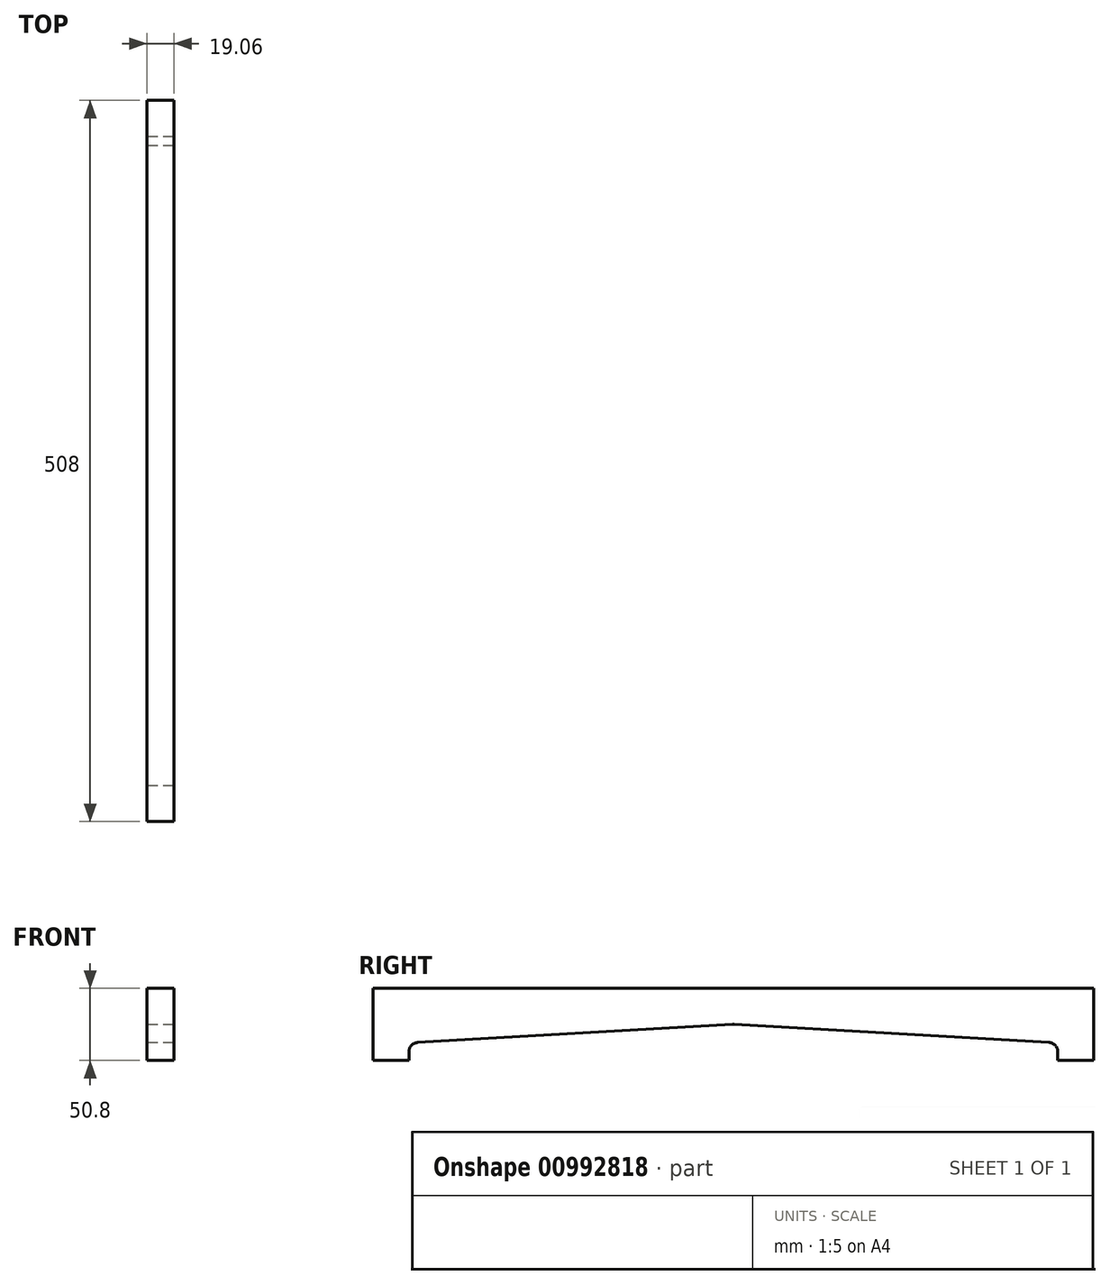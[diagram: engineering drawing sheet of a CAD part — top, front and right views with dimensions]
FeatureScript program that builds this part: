
annotation { "Feature Type Name" : "Feature", "Feature Type Description" : "" }
export const myFeature = defineFeature(function(context is Context, id is Id, definition is map)
    precondition{}
    {
        {
            var Q0;
            Q0=qCreatedBy(makeId("Front.planeOp"),FACE);
            var sketch = newSketch(context, id + "F0", { "sketchPlane" : qUnion([Q0])});
            skLineSegment(sketch, "E0", {"start": v(0, 25.4) * mm, "end": v(0, -25.4) * mm, "construction": true});
            skLineSegment(sketch, "E1", {"start": v(9.52, 0) * mm, "end": v(-9.52, 0) * mm, "construction": true});
            skLineSegment(sketch, "E2.bottom", {"start": v(9.52, 25.4) * mm, "end": v(-9.52, 25.4) * mm});
            skLineSegment(sketch, "E2.top", {"start": v(9.52, -25.4) * mm, "end": v(-9.52, -25.4) * mm});
            skLineSegment(sketch, "E2.left", {"start": v(9.52, 25.4) * mm, "end": v(9.52, -25.4) * mm});
            skLineSegment(sketch, "E2.right", {"start": v(-9.52, 25.4) * mm, "end": v(-9.52, -25.4) * mm});
            skPoint(sketch, "E2.middle", {"position": v(0, 0) * mm});
            skSolve(sketch);
        }
        {
            var Q0;
            Q0 = qSketchRegion(id + "F0", true);
            extrude(context, id + "F1", {"entities" : qUnion([Q0]), "endBound" : BoundingType.SYMMETRIC, "depth" : 508 * mm, "offsetDistance" : 25.4 * mm});
        }
        {
            var Q0;
            Q0=makeQuery(id+"F1.opExtrude","SWEPT_FACE",FACE,{"disambiguationData":[OSD([sQuery(id+"F0.wireOp",EDGE,"E2.left")])]});
            var sketch = newSketch(context, id + "F2", { "sketchPlane" : qUnion([Q0])});
            skLineSegment(sketch, "E3", {"start": v(-254, 0) * mm, "end": v(254, 0) * mm, "construction": true});
            skLineSegment(sketch, "E4", {"start": v(254, 0) * mm, "end": v(254, -25.4) * mm, "construction": true});
            skLineSegment(sketch, "E5", {"start": v(-254, -25.4) * mm, "end": v(-254, 0) * mm, "construction": true});
            skLineSegment(sketch, "E6", {"start": v(-254, -12.7) * mm, "end": v(254, -12.7) * mm, "construction": true});
            skLineSegment(sketch, "E7", {"start": v(0, -25.4) * mm, "end": v(0, 25.4) * mm, "construction": true});
            skLineSegment(sketch, "E8", {"start": v(0, 25.4) * mm, "end": v(254, 25.4) * mm, "construction": true});
            skLineSegment(sketch, "E9", {"start": v(-254, 25.4) * mm, "end": v(0, 25.4) * mm, "construction": true});
            skLineSegment(sketch, "E10", {"start": v(-127, 25.4) * mm, "end": v(-127, -25.4) * mm, "construction": true});
            skLineSegment(sketch, "E11", {"start": v(127, 25.4) * mm, "end": v(127, -25.4) * mm, "construction": true});
            skLineSegment(sketch, "E12", {"start": v(-228.6, -25.4) * mm, "end": v(-228.6, 25.4) * mm, "construction": true});
            skLineSegment(sketch, "E13", {"start": v(228.6, -25.4) * mm, "end": v(228.6, 25.4) * mm, "construction": true});
            skLineSegment(sketch, "E14.0", {"start": v(-254, 25.4) * mm, "end": v(-254, -25.4) * mm});
            skCircle(sketch, "E15", {"center": v(0, -12.7) * mm, "radius": 12.7 * mm});
            skCircle(sketch, "E16", {"center": v(-222.25, -19.05) * mm, "radius": 6.35 * mm});
            skCircle(sketch, "E17", {"center": v(222.25, -19.05) * mm, "radius": 6.35 * mm});
            skLineSegment(sketch, "E18", {"start": v(0.73, -0.02) * mm, "end": v(222.25, -12.7) * mm});
            skLineSegment(sketch, "E19", {"start": v(-222.61, -12.71) * mm, "end": v(-0.73, -0.02) * mm});
            skLineSegment(sketch, "E20", {"start": v(228.6, -25.4) * mm, "end": v(228.6, -19.05) * mm});
            skLineSegment(sketch, "E21", {"start": v(-228.6, -25.4) * mm, "end": v(-228.6, -19.05) * mm});
            skSolve(sketch);
        }
        {
            var Q0;
            Q0 = qSketchRegion(id + "F2", true);
            var Q1;
            {var subQ0=sQuery(id+"F2.wireOp",EDGE,"E19");Q1=makeQuery(id+"F2.imprint","IMPRINT",FACE,{"disambiguationData":[TD([[makeQuery(id+"F2.imprint","IMPRINT",EDGE,{"derivedFrom":subQ0}),-1.0]])]});}
            var Q2;
            {var subQ0=sQuery(id+"F2.wireOp",EDGE,"E18");Q2=makeQuery(id+"F2.imprint","IMPRINT",FACE,{"disambiguationData":[TD([[makeQuery(id+"F2.imprint","IMPRINT",EDGE,{"derivedFrom":subQ0}),-1.0]])]});}
            var Q3;
            {var subQ0=sQuery(id+"F2.wireOp",EDGE,"E20");Q3=makeQuery(id+"F2.imprint","IMPRINT",FACE,{"disambiguationData":[TD([[makeQuery(id+"F2.imprint","IMPRINT",EDGE,{"derivedFrom":subQ0}),1.0]])]});}
            var Q4;
            {var subQ0=sQuery(id+"F2.wireOp",EDGE,"E21");Q4=makeQuery(id+"F2.imprint","IMPRINT",FACE,{"disambiguationData":[TD([[makeQuery(id+"F2.imprint","IMPRINT",EDGE,{"derivedFrom":subQ0}),-1.0]])]});}
            extrude(context, id + "F3", {"entities" : qUnion([Q0, Q1, Q2, Q3, Q4]), "operationType" : NewBodyOperationType.REMOVE, "endBound" : BoundingType.THROUGH_ALL, "oppositeDirection" : true, "depth" : 25.4 * mm, "offsetDistance" : 25.4 * mm});
        }
    });
